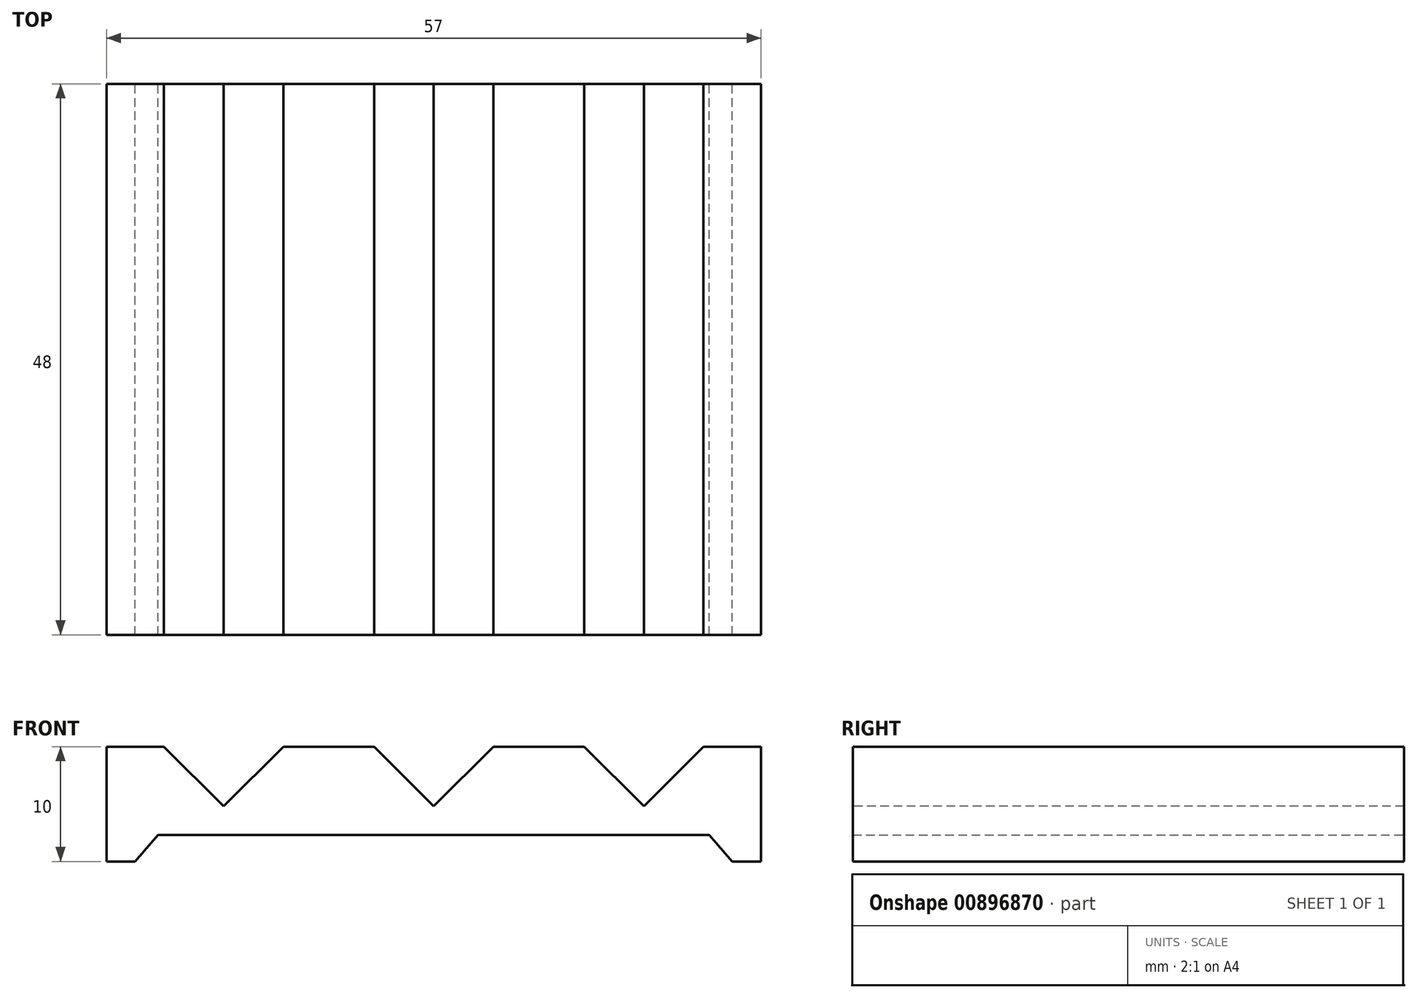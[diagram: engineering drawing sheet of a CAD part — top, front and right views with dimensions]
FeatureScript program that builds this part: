
annotation { "Feature Type Name" : "Feature", "Feature Type Description" : "" }
export const myFeature = defineFeature(function(context is Context, id is Id, definition is map)
    precondition{}
    {
        {
            var Q0;
            Q0=qCreatedBy(makeId("Front.planeOp"),FACE);
            var sketch = newSketch(context, id + "F0", { "sketchPlane" : qUnion([Q0])});
            skLineSegment(sketch, "E0", {"start": v(-28.5, 0) * mm, "end": v(-28.5, 10) * mm});
            skLineSegment(sketch, "E1", {"start": v(-28.5, 10) * mm, "end": v(28.5, 10) * mm});
            skLineSegment(sketch, "E2", {"start": v(28.5, 10) * mm, "end": v(28.5, 0) * mm});
            skLineSegment(sketch, "E3", {"start": v(28.5, 0) * mm, "end": v(26, 0) * mm});
            skLineSegment(sketch, "E4", {"start": v(26, 0) * mm, "end": v(24, 2.3) * mm});
            skLineSegment(sketch, "E5", {"start": v(-24, 2.3) * mm, "end": v(24, 2.3) * mm});
            skLineSegment(sketch, "E6", {"start": v(-24, 2.3) * mm, "end": v(-26, 0) * mm});
            skLineSegment(sketch, "E7", {"start": v(-28.5, 0) * mm, "end": v(-26, 0) * mm});
            skSolve(sketch);
        }
        {
            var Q0;
            Q0=makeQuery(id+"F0.imprint","IMPRINT",FACE,{"disambiguationData":[TD([[makeQuery(id+"F0.imprint","IMPRINT",EDGE,{"derivedFrom":sQuery(id+"F0.wireOp",EDGE,"E0")}),-1.0]])]});
            extrude(context, id + "F1", {"entities" : qUnion([Q0]), "endBound" : BoundingType.SYMMETRIC, "depth" : 48 * mm, "offsetDistance" : 25 * mm});
        }
        {
            var Q0;
            Q0=makeQuery(id+"F1.opExtrude","SWEPT_FACE",FACE,{"disambiguationData":[OSD([sQuery(id+"F0.wireOp",EDGE,"E1")])]});
            cPlane(context, id + "F2", {"entities" : qUnion([Q0]), "cplaneType" : CPlaneType.OFFSET, "offset" : 0 * mm, "width" : 150 * mm, "height" : 150 * mm});
        }
        {
            var Q0;
            Q0=qCreatedBy(id+"F2.planeOp",FACE);
            var sketch = newSketch(context, id + "F3", { "sketchPlane" : qUnion([Q0])});
            skLineSegment(sketch, "E8.bottom", {"start": v(-23.5, -24) * mm, "end": v(-13.1, -24) * mm});
            skLineSegment(sketch, "E8.top", {"start": v(-23.5, 24) * mm, "end": v(-13.1, 24) * mm});
            skLineSegment(sketch, "E8.left", {"start": v(-23.5, -24) * mm, "end": v(-23.5, 24) * mm});
            skLineSegment(sketch, "E8.right", {"start": v(-13.1, -24) * mm, "end": v(-13.1, 24) * mm});
            skLineSegment(sketch, "E9.1.0.0", {"start": v(-5.2, 24) * mm, "end": v(5.2, 24) * mm});
            skLineSegment(sketch, "E9.1.0.1", {"start": v(5.2, -24) * mm, "end": v(5.2, 24) * mm});
            skLineSegment(sketch, "E9.1.0.2", {"start": v(-5.2, -24) * mm, "end": v(-5.2, 24) * mm});
            skLineSegment(sketch, "E9.1.0.3", {"start": v(-5.2, -24) * mm, "end": v(5.2, -24) * mm});
            skLineSegment(sketch, "E9.2.0.0", {"start": v(13.1, 24) * mm, "end": v(23.5, 24) * mm});
            skLineSegment(sketch, "E9.2.0.1", {"start": v(23.5, -24) * mm, "end": v(23.5, 24) * mm});
            skLineSegment(sketch, "E9.2.0.2", {"start": v(13.1, -24) * mm, "end": v(13.1, 24) * mm});
            skLineSegment(sketch, "E9.2.0.3", {"start": v(13.1, -24) * mm, "end": v(23.5, -24) * mm});
            skLineSegment(sketch, "E9.direction1", {"start": v(-23.5, 24) * mm, "end": v(-5.2, 24) * mm, "construction": true});
            skSolve(sketch);
        }
        {
            var Q0;
            Q0 = qSketchRegion(id + "F3", true);
            extrude(context, id + "F4", {"entities" : qUnion([Q0]), "operationType" : NewBodyOperationType.REMOVE, "oppositeDirection" : true, "depth" : 5.2 * mm, "offsetDistance" : 25 * mm});
        }
        {
            var Q0;
            Q0=makeQuery(id+"F4.boolean.opBoolean","COPY",EDGE,{"derivedFrom":makeQuery(id+"F4.opExtrude","CAP_EDGE",EDGE,{"disambiguationData":[OSD([sQuery(id+"F3.wireOp",EDGE,"E8.right")])],"isStart":false})});
            var Q1;
            Q1=makeQuery(id+"F4.boolean.opBoolean","COPY",EDGE,{"derivedFrom":makeQuery(id+"F4.opExtrude","CAP_EDGE",EDGE,{"disambiguationData":[OSD([sQuery(id+"F3.wireOp",EDGE,"E8.left")])],"isStart":false})});
            var Q2;
            Q2=makeQuery(id+"F4.boolean.opBoolean","COPY",EDGE,{"derivedFrom":makeQuery(id+"F4.opExtrude","CAP_EDGE",EDGE,{"disambiguationData":[OSD([sQuery(id+"F3.wireOp",EDGE,"E9.1.0.2")])],"isStart":false})});
            var Q3;
            Q3=makeQuery(id+"F4.boolean.opBoolean","COPY",EDGE,{"derivedFrom":makeQuery(id+"F4.opExtrude","CAP_EDGE",EDGE,{"disambiguationData":[OSD([sQuery(id+"F3.wireOp",EDGE,"E9.1.0.1")])],"isStart":false})});
            var Q4;
            Q4=makeQuery(id+"F4.boolean.opBoolean","COPY",EDGE,{"derivedFrom":makeQuery(id+"F4.opExtrude","CAP_EDGE",EDGE,{"disambiguationData":[OSD([sQuery(id+"F3.wireOp",EDGE,"E9.2.0.2")])],"isStart":false})});
            var Q5;
            Q5=makeQuery(id+"F4.boolean.opBoolean","COPY",EDGE,{"derivedFrom":makeQuery(id+"F4.opExtrude","CAP_EDGE",EDGE,{"disambiguationData":[OSD([sQuery(id+"F3.wireOp",EDGE,"E9.2.0.1")])],"isStart":false})});
            chamfer(context, id + "F5", {"entities" : qUnion([Q0, Q1, Q2, Q3, Q4, Q5]), "width" : 5.2 * mm, "tangentPropagation" : true});
        }
    });
